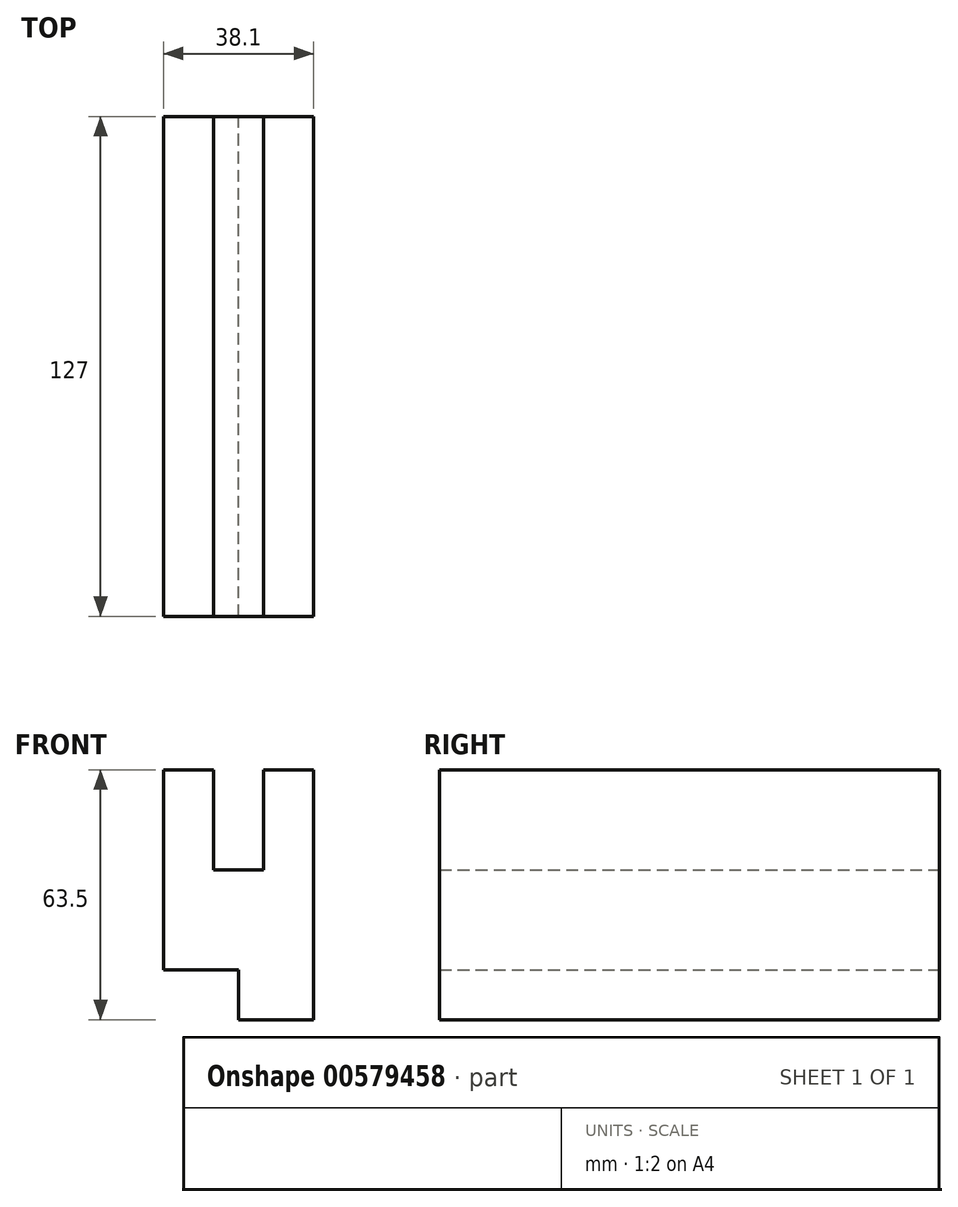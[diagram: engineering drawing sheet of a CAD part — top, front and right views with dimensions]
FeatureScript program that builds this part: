
annotation { "Feature Type Name" : "Feature", "Feature Type Description" : "" }
export const myFeature = defineFeature(function(context is Context, id is Id, definition is map)
    precondition{}
    {
        {
            var Q0;
            Q0=qCreatedBy(makeId("Front.planeOp"),FACE);
            var sketch = newSketch(context, id + "F0", { "sketchPlane" : qUnion([Q0])});
            skLineSegment(sketch, "E0", {"start": v(-25.43, 25.23) * mm, "end": v(-25.43, -25.57) * mm});
            skLineSegment(sketch, "E1", {"start": v(-25.43, -25.57) * mm, "end": v(-6.38, -25.57) * mm});
            skLineSegment(sketch, "E2", {"start": v(-6.38, -25.57) * mm, "end": v(-6.38, -38.27) * mm});
            skLineSegment(sketch, "E3", {"start": v(-6.38, -38.27) * mm, "end": v(12.67, -38.27) * mm});
            skLineSegment(sketch, "E4", {"start": v(12.67, -38.27) * mm, "end": v(12.67, 25.23) * mm});
            skLineSegment(sketch, "E5", {"start": v(12.67, 25.23) * mm, "end": v(-0.03, 25.23) * mm});
            skLineSegment(sketch, "E6", {"start": v(-0.03, 25.23) * mm, "end": v(-0.03, -0.17) * mm});
            skLineSegment(sketch, "E7", {"start": v(-0.03, -0.17) * mm, "end": v(-12.73, -0.17) * mm});
            skLineSegment(sketch, "E8", {"start": v(-12.73, -0.17) * mm, "end": v(-12.73, 25.23) * mm});
            skLineSegment(sketch, "E9", {"start": v(-12.73, 25.23) * mm, "end": v(-25.43, 25.23) * mm});
            skSolve(sketch);
        }
        {
            var Q0;
            Q0 = qSketchRegion(id + "F0", true);
            extrude(context, id + "F1", {"entities" : qUnion([Q0]), "depth" : 127 * mm, "offsetDistance" : 25.4 * mm});
        }
    });
